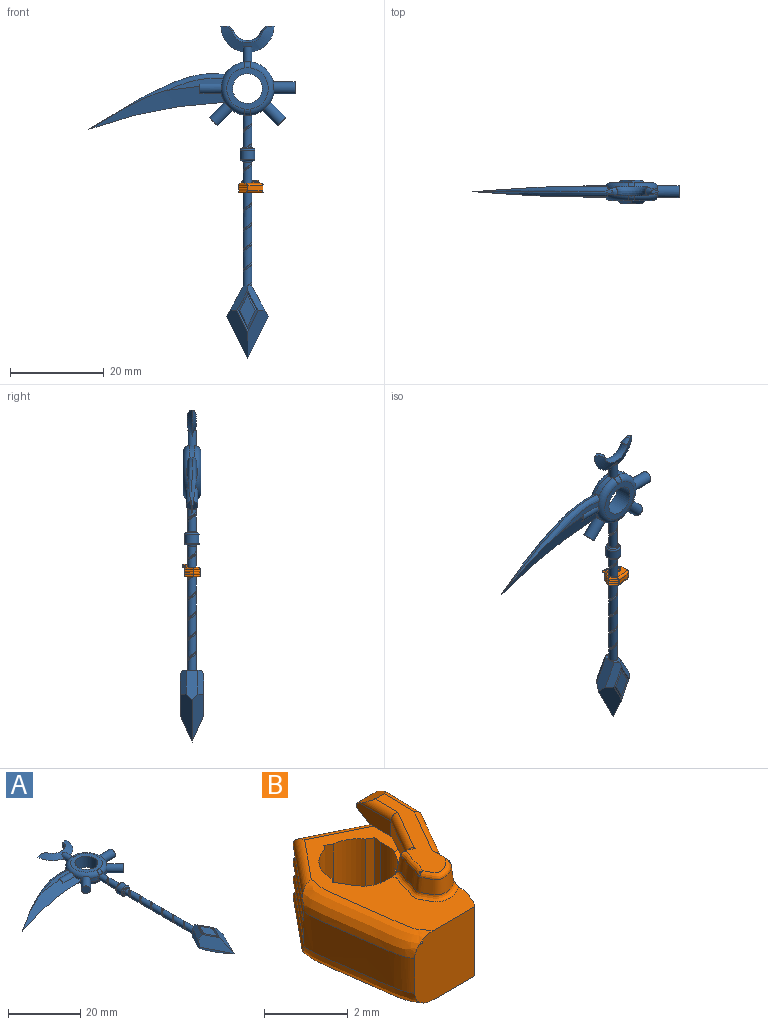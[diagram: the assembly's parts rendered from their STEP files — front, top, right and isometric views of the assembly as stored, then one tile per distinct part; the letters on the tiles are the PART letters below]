
ASSEMBLY  parts=2 mates=1
PART A: 95 faces, bbox 47.1x71.3x5.4 mm
  f0: cylinder r=0.95mm len=6.92mm, axis (0,1,0), area 36.3mm2, adj f1,f2,f3,f6,f20,f23,f67,f69
  f1: bspline ~8.16x2.41mm, area 3.9mm2, adj f0,f2,f3,f37,f38,f67,f68,f69
  f2: bspline ~8.15x2.45mm, area 3.9mm2, adj f0,f1,f20,f37,f38,f67
  f3: cylinder r=5.71mm len=2.59mm, axis (0,0,-1), area 3.2mm2, adj f0,f1,f12,f13,f35,f37
  f4: cylinder r=5.71mm len=2.11mm, axis (0,0,-1), area 0.8mm2, adj f13,f35,f40,f44
  f5: cylinder r=3.17mm len=6.35mm, axis (0,0,-1), area 76mm2, adj f16,f17
  f6: cylinder r=5.71mm len=2.59mm, axis (0,0,-1), area 3.2mm2, adj f0,f8,f9,f33
  f7: cylinder r=5.71mm len=2.11mm, axis (0,0,-1), area 2.6mm2, adj f8,f9,f25,f33
  f8: torus R=4.45mm, axis (0,0,1), area 28.3mm2, adj f6,f7,f15,f17,f20,f21,f25,f33
  f9: torus R=4.45mm, axis (0,0,1), area 28.3mm2, adj f6,f7,f15,f16,f22,f23,f25,f33
  f10: cylinder r=5.71mm len=4.27mm, axis (0,0,-1), area 6.4mm2, adj f12,f13,f19,f41,f42
  f11: cylinder r=5.71mm len=2.11mm, axis (0,0,-1), area 0.8mm2, adj f12,f35,f39,f45
  f12: torus R=4.45mm, axis (0,0,1), area 27.6mm2, adj f3,f10,f11,f17,f20,f21,f32,f35
  f13: torus R=4.45mm, axis (0,0,1), area 27.7mm2, adj f3,f4,f10,f16,f22,f23,f31,f35
  f14: plane 1.74x0.58mm, normal (0,1,0), area 0.4mm2, adj f19,f26
  f15: cylinder r=5.71mm len=4.87mm, axis (0,0,-1), area 8.6mm2, adj f8,f9,f19,f25
  f16: plane 8.97x8.89mm, normal (0,0,1), area 30.4mm2, adj f5,f9,f13,f22,f23
  f17: plane 8.97x8.89mm, normal (0,0,-1), area 30.4mm2, adj f5,f8,f12,f20,f21
  f18: plane 1.66x0.52mm, normal (0,1,0), area 0.4mm2, adj f19,f27
  f19: cylinder r=0.95mm len=3.3mm, axis (0,1,0), area 18.3mm2, adj f10,f14,f15,f18,f21,f22,f26,f27
  f20: bspline ~1.53x1.35mm, area 2.3mm2, adj f0,f2,f8,f12,f17,f37
  f21: bspline ~1.42x1.3mm, area 2.3mm2, adj f8,f12,f17,f19
  f22: bspline ~1.42x1.3mm, area 2.3mm2, adj f9,f13,f16,f19
  f23: bspline ~1.42x1.3mm, area 2.3mm2, adj f0,f9,f13,f16
  f24: plane 2.54x2.54mm, normal (1,0,0), area 5.1mm2, adj f25
  f25: cylinder r=1.27mm len=4.58mm, axis (-1,0,0), area 36.3mm2, adj f7,f8,f9,f15,f24
  f26: bspline ~11.33x5.46mm, area 29.7mm2, adj f14,f19,f27,f28,f29,f30,f93,f94
  f27: bspline ~11.33x5.46mm, area 30.2mm2, adj f18,f19,f26,f28,f29,f30,f93,f94
  f28: plane 1.88x1.27mm, normal (0.01,1,0), area 0.8mm2, adj f26,f27,f94
  f29: plane 1.84x1.25mm, normal (0.01,1,0), area 0.7mm2, adj f26,f27,f93
  f30: bspline ~7.14x7.14mm, area 18.5mm2, adj f26,f27,f93,f94
  f31: plane 12.18x2.8mm, normal (0,0,1), area 11.7mm2, adj f13,f40,f41,f43,f44
  f32: plane 12.19x2.81mm, normal (0,0,-1), area 11.7mm2, adj f12,f39,f42,f45,f46
  f33: cylinder r=1.27mm len=5.04mm, axis (-0.71,0.71,0), area 36.3mm2, adj f6,f7,f8,f9,f34
  f34: plane 2.54x1.8mm, normal (0.71,-0.71,0), area 5.1mm2, adj f33
  f35: cylinder r=1.27mm len=5.06mm, axis (0.71,0.71,0), area 36.2mm2, adj f3,f4,f11,f12,f13,f36
  f36: plane 2.54x1.8mm, normal (-0.71,-0.71,0), area 5.1mm2, adj f35
  f37: bspline ~2.13x1.59mm, area 0.5mm2, adj f1,f2,f3,f12,f20,f38
  f38: plane 0.71x0.37mm, normal (0,0,-1), area 0.1mm2, adj f1,f2,f37
  f39: bspline ~33.29x10.15mm, area 73.1mm2, adj f11,f32,f40,f42,f45,f46
  f40: bspline ~33.29x10.15mm, area 73mm2, adj f4,f31,f39,f41,f43,f44
  f41: bspline ~30.28x13.43mm, area 35.4mm2, adj f10,f13,f31,f40,f42
  f42: bspline ~30.28x13.43mm, area 35.4mm2, adj f10,f12,f32,f39,f41
  f43: plane 1.87x0.64mm, normal (-1,0,0), area 0.5mm2, adj f31,f40,f44
  f44: cylinder r=1.27mm len=4.58mm, axis (1,0,0), area 10.1mm2, adj f4,f13,f31,f40,f43
  f45: cylinder r=1.27mm len=4.58mm, axis (1,0,0), area 10.1mm2, adj f11,f12,f32,f39,f46
  f46: plane 1.87x0.64mm, normal (-1,0,0), area 0.5mm2, adj f32,f39,f45
  f47: plane 2.57x2.57mm, normal (0,1,0), area 0.2mm2, adj f67,f68,f69,f74
  f48: plane 2.57x2.57mm, normal (0,-1,0), area 0.2mm2, adj f70,f71,f72,f73
  f49: cylinder r=1.59mm len=3.18mm, axis (0,-1,0), area 19.3mm2, adj f73,f74
  f50: plane 10.2x4.46mm, normal (-0.63,-0.32,0.71), area 28.3mm2, adj f51,f53,f57,f58,f78
  f51: plane 10.2x4.46mm, normal (-0.63,-0.32,-0.71), area 28.3mm2, adj f50,f52,f55,f58,f84
  f52: plane 5.16x3.72mm, normal (-0.62,0.34,-0.71), area 10.1mm2, adj f51,f54,f58,f59,f85
  f53: plane 10.2x4.46mm, normal (0.63,-0.32,0.71), area 28.3mm2, adj f50,f55,f56,f61,f79
  f54: plane 5.16x3.72mm, normal (0.62,0.34,-0.71), area 10.1mm2, adj f52,f55,f60,f61,f86
  f55: plane 10.2x4.46mm, normal (0.63,-0.32,-0.71), area 28.3mm2, adj f51,f53,f54,f61,f91
  f56: plane 5.16x3.72mm, normal (0.62,0.34,0.71), area 10.1mm2, adj f53,f57,f61,f62,f80
  f57: plane 5.16x3.72mm, normal (-0.62,0.34,0.71), area 10.1mm2, adj f50,f56,f58,f63,f81
  f58: plane 6.48x3.56mm, normal (-0.88,0.48,0), area 16.7mm2, adj f50,f51,f52,f57,f59,f63,f66
  f59: plane 1.93x0.96mm, normal (-0.06,1,0), area 0.9mm2, adj f52,f58,f60,f66
  f60: plane 1.93x0.96mm, normal (0.06,1,0), area 0.9mm2, adj f54,f59,f61,f66
  f61: plane 6.48x3.56mm, normal (0.88,0.48,0), area 16.7mm2, adj f53,f54,f55,f56,f60,f62,f66
  f62: plane 1.94x0.96mm, normal (0.06,1,0), area 0.9mm2, adj f56,f61,f63,f64,f65,f66
  f63: plane 1.93x0.95mm, normal (-0.06,1,0), area 0.9mm2, adj f57,f58,f62,f64,f66
  f64: bspline ~28x2.45mm, area 13.4mm2, adj f62,f63,f65,f66,f70,f71,f72
  f65: bspline ~28.02x2.41mm, area 13.8mm2, adj f62,f64,f66,f71
  f66: cylinder r=0.95mm len=26.59mm, axis (0,1,0), area 134.4mm2, adj f58,f59,f60,f61,f62,f63,f64,f65
  f67: bspline ~0.85x0.81mm, area 0.2mm2, adj f0,f1,f2,f47,f68,f69
  f68: bspline ~0.61x0.46mm, area 0.1mm2, adj f1,f47,f67,f69
  f69: torus R=1.26mm, axis (0,-1,0), area 3mm2, adj f0,f1,f47,f67,f68
  f70: bspline ~0.57x0.49mm, area 0.1mm2, adj f48,f64,f71,f72
  f71: bspline ~0.85x0.75mm, area 0.2mm2, adj f48,f64,f65,f66,f70,f72
  f72: torus R=1.26mm, axis (0,-1,0), area 3mm2, adj f48,f64,f66,f70,f71
  f73: torus R=1.28mm, axis (0,-1,0), area 4.4mm2, adj f48,f49
  f74: torus R=1.28mm, axis (0,-1,0), area 4.4mm2, adj f47,f49
  f75: plane 3.66x2mm, normal (-0.62,0.34,0.71), area 1.4mm2, adj f76,f81,f82,f83
  f76: plane 3.66x2mm, normal (0.62,0.34,0.71), area 1.4mm2, adj f75,f77,f80,f83
  f77: plane 3.96x2mm, normal (0.63,-0.32,0.71), area 1.5mm2, adj f76,f79,f82,f83
  f78: plane 4.53x2.28mm, normal (0.63,0.32,0.71), area 1.7mm2, adj f50,f79,f81,f82
  f79: plane 4.53x2.28mm, normal (-0.63,0.32,0.71), area 1.7mm2, adj f53,f77,f78,f80
  f80: plane 4.18x2.28mm, normal (-0.62,-0.34,0.71), area 1.6mm2, adj f56,f76,f79,f81
  f81: plane 4.18x2.28mm, normal (0.62,-0.34,0.71), area 1.6mm2, adj f57,f75,f78,f80
  f82: plane 3.96x2mm, normal (-0.63,-0.32,0.71), area 1.5mm2, adj f75,f77,f78,f83
  f83: plane 6.52x3.42mm, normal (0,0,1), area 11.1mm2, adj f75,f76,f77,f82
  f84: plane 4.53x2.28mm, normal (0.63,0.32,-0.71), area 1.7mm2, adj f51,f85,f90,f91
  f85: plane 4.18x2.28mm, normal (0.62,-0.34,-0.71), area 1.6mm2, adj f52,f84,f86,f89
  f86: plane 4.18x2.28mm, normal (-0.62,-0.34,-0.71), area 1.6mm2, adj f54,f85,f88,f91
  f87: plane 3.96x2mm, normal (0.63,-0.32,-0.71), area 1.5mm2, adj f88,f90,f91,f92
  f88: plane 3.66x2mm, normal (0.62,0.34,-0.71), area 1.4mm2, adj f86,f87,f89,f92
  f89: plane 3.66x2mm, normal (-0.62,0.34,-0.71), area 1.4mm2, adj f85,f88,f90,f92
  f90: plane 3.96x2mm, normal (-0.63,-0.32,-0.71), area 1.5mm2, adj f84,f87,f89,f92
  f91: plane 4.53x2.28mm, normal (-0.63,0.32,-0.71), area 1.7mm2, adj f55,f84,f86,f87
  f92: plane 6.52x3.42mm, normal (0,0,-1), area 11.1mm2, adj f87,f88,f89,f90
  f93: bspline ~2.68x1.63mm, area 2.6mm2, adj f26,f27,f29,f30
  f94: bspline ~2.79x1.69mm, area 2.8mm2, adj f26,f27,f28,f30
PART B: 79 faces, bbox 4.3x5.7x2.9 mm
  f0: plane 4.84x2.76mm, normal (0,0,-1), area 6.7mm2, adj f5,f6,f7,f8,f9,f10,f12,f16
  f1: plane 0.22x0.13mm, normal (-0.98,0.2,0), area 0mm2, adj f10,f19,f23,f76
  f2: plane 0.22x0.13mm, normal (-0.98,0.2,0), area 0mm2, adj f25,f29,f30,f76
  f3: plane 0.22x0.13mm, normal (-0.98,0.2,0), area 0mm2, adj f32,f36,f37,f76
  f4: plane 0.22x0.13mm, normal (-0.98,0.2,0), area 0mm2, adj f39,f43,f44,f76
  f5: plane 2.03x0.23mm, normal (-0.98,0.2,0), area 0.5mm2, adj f0,f7,f11,f76
  f6: plane 2.03x0.21mm, normal (-0.51,-0.86,0), area 0.5mm2, adj f0,f9,f11,f78
  f7: plane 2.03x0.2mm, normal (-0.51,-0.86,0), area 0.5mm2, adj f0,f5,f11,f78
  f8: plane 2.03x0.12mm, normal (0.8,-0.6,0), area 0.3mm2, adj f0,f11,f12,f77
  f9: plane 2.03x0.14mm, normal (0.8,-0.6,0), area 0.4mm2, adj f0,f6,f11,f77
  f10: plane 0.47x0.41mm, normal (-0.04,-0.5,-0.87), area 0.2mm2, adj f0,f1,f19,f24,f76
  f11: plane 4.94x2.78mm, normal (0,0,1), area 5.2mm2, adj f5,f6,f7,f8,f9,f12,f16,f17
  f12: extruded ~2.03x2.02mm, area 5mm2, adj f0,f8,f11,f17,f48,f69
  f13: extruded ~0.41x0.37mm, area 0.1mm2, adj f18,f35,f42,f46
  f14: extruded ~0.51x0.37mm, area 0.1mm2, adj f18,f28,f35
  f15: extruded ~0.41x0.37mm, area 0.1mm2, adj f18,f22,f28,f47
  f16: plane 2.18x2.18mm, normal (0,-1,0), area 4mm2, adj f0,f11,f17,f18,f46,f47
  f17: extruded ~2.05x2.01mm, area 4.2mm2, adj f0,f11,f12,f16,f48,f70,f72
  f18: extruded ~3.28x1.02mm, area 3.4mm2, adj f13,f14,f15,f16,f46,f47
  f19: plane 0.48x0.07mm, normal (-0.07,-1,0), area 0mm2, adj f1,f10,f23,f24
  f20: cylinder r=0.25mm len=1.12mm, axis (0.14,0.99,0), area 0.9mm2, adj f0,f21,f24,f26
  f21: cylinder r=0.25mm len=1.76mm, axis (-0.9,0.44,0), area 1.5mm2, adj f0,f20,f22,f27
  f22: cylinder r=0.25mm len=2.02mm, axis (-0.64,-0.77,0), area 1.7mm2, adj f0,f15,f21,f28,f47
  f23: plane 0.47x0.41mm, normal (-0.04,-0.5,0.87), area 0.2mm2, adj f1,f19,f24,f29,f76
  f24: bspline ~0.52x0.38mm, area 0.2mm2, adj f10,f19,f20,f23
  f25: plane 0.48x0.07mm, normal (-0.07,-1,0), area 0mm2, adj f2,f29,f30,f31
  f26: cylinder r=0.25mm len=1.12mm, axis (0.14,0.99,0), area 0.9mm2, adj f20,f27,f31,f33
  f27: cylinder r=0.25mm len=1.76mm, axis (-0.9,0.44,0), area 1.5mm2, adj f21,f26,f28,f34
  f28: cylinder r=0.25mm len=1.88mm, axis (-0.64,-0.77,0), area 1.7mm2, adj f14,f15,f22,f27,f35
  f29: plane 0.47x0.41mm, normal (-0.04,-0.5,-0.87), area 0.2mm2, adj f2,f23,f25,f31,f76
  f30: plane 0.47x0.41mm, normal (-0.04,-0.5,0.87), area 0.2mm2, adj f2,f25,f31,f36,f76
  f31: bspline ~0.52x0.38mm, area 0.2mm2, adj f25,f26,f29,f30
  f32: plane 0.48x0.07mm, normal (-0.07,-1,0), area 0mm2, adj f3,f36,f37,f38
  f33: cylinder r=0.25mm len=1.12mm, axis (0.14,0.99,0), area 0.9mm2, adj f26,f34,f38,f40
  f34: cylinder r=0.25mm len=1.76mm, axis (-0.9,0.44,0), area 1.5mm2, adj f27,f33,f35,f41
  f35: cylinder r=0.25mm len=1.88mm, axis (-0.64,-0.77,0), area 1.7mm2, adj f13,f14,f28,f34,f42
  f36: plane 0.47x0.41mm, normal (-0.04,-0.5,-0.87), area 0.2mm2, adj f3,f30,f32,f38,f76
  f37: plane 0.47x0.41mm, normal (-0.04,-0.5,0.87), area 0.2mm2, adj f3,f32,f38,f43,f76
  f38: bspline ~0.52x0.38mm, area 0.2mm2, adj f32,f33,f36,f37
  f39: plane 0.48x0.07mm, normal (-0.07,-1,0), area 0mm2, adj f4,f43,f44,f45
  f40: cylinder r=0.25mm len=1.3mm, axis (-0.14,-0.99,0), area 1mm2, adj f11,f33,f41,f45,f48
  f41: cylinder r=0.25mm len=2.11mm, axis (0.9,-0.44,0), area 1.7mm2, adj f11,f34,f40,f42,f48
  f42: cylinder r=0.25mm len=2.02mm, axis (0.64,0.77,0), area 1.7mm2, adj f11,f13,f35,f41,f46
  f43: plane 0.47x0.41mm, normal (-0.04,-0.5,-0.87), area 0.2mm2, adj f4,f37,f39,f45,f76
  f44: plane 0.48x0.41mm, normal (-0.04,-0.5,0.87), area 0.2mm2, adj f4,f11,f39,f45,f48,f76
  f45: bspline ~0.52x0.38mm, area 0.2mm2, adj f39,f40,f43,f44
  f46: bspline ~4.29x1.18mm, area 2.8mm2, adj f11,f13,f16,f18,f42
  f47: bspline ~4.29x1.18mm, area 2.8mm2, adj f0,f15,f16,f18,f22
  f48: plane 2.43x1.13mm, normal (0,0,-1), area 1mm2, adj f12,f17,f40,f41,f44,f54,f56,f61
  f49: extruded ~0.25x0.05mm, area 0mm2, adj f51,f54,f57,f69
  f50: plane 0.25x0.17mm, normal (0.87,-0.5,0), area 0mm2, adj f52,f55,f58,f70
  f51: bspline ~1.04x0.65mm, area 0mm2, adj f49,f62,f66,f69
  f52: cylinder r=0.19mm len=0.24mm, axis (-0.5,-0.87,0), area 0mm2, adj f50,f53,f70
  f53: cylinder r=0.19mm len=1.64mm, axis (-0.5,-0.87,0), area 0.5mm2, adj f52,f58,f62,f67,f70
  f54: bspline ~3.19x1.76mm, area 0.3mm2, adj f11,f48,f49,f57,f61,f69
  f55: cylinder r=0.19mm len=0.14mm, axis (0.5,0.87,0), area 0mm2, adj f50,f56,f70
  f56: cylinder r=0.19mm len=1.64mm, axis (0.5,0.87,0), area 0.5mm2, adj f48,f55,f58,f68,f70
  f57: plane 1.26x0.73mm, normal (-0.87,0.5,0), area 0.5mm2, adj f49,f54,f61,f66
  f58: plane 1.54x0.89mm, normal (0.87,-0.5,0), area 0.5mm2, adj f50,f53,f56,f59
  f59: plane 1.54x0.25mm, normal (1,-0.03,0), area 0.4mm2, adj f58,f60,f63,f64,f67,f68
  f60: plane 0.7x0.13mm, normal (0,1,0), area 0.1mm2, adj f59,f61,f63,f64
  f61: plane 1.42x0.45mm, normal (-1,0,0), area 0.5mm2, adj f11,f48,f54,f57,f60,f63,f64,f65
  f62: plane 3.34x1.7mm, normal (0,0,1), area 1.5mm2, adj f51,f53,f64,f65,f66,f67,f69,f70
  f63: plane 0.84x0.58mm, normal (0,0.5,-0.87), area 0.3mm2, adj f48,f59,f60,f61,f68
  f64: plane 0.84x0.58mm, normal (0,0.5,0.87), area 0.3mm2, adj f59,f60,f61,f62,f65,f67
  f65: cylinder r=0.19mm len=1.1mm, axis (0,1,0), area 0.3mm2, adj f61,f62,f64,f66
  f66: cylinder r=0.19mm len=1.4mm, axis (0.5,0.87,0), area 0.4mm2, adj f51,f57,f62,f65
  f67: cylinder r=0.19mm len=1.44mm, axis (-0.03,-1,0), area 0.4mm2, adj f53,f59,f62,f64
  f68: cylinder r=0.19mm len=1.44mm, axis (0.03,1,0), area 0.4mm2, adj f48,f56,f59,f63
  f69: bspline ~0.7x0.69mm, area 0.2mm2, adj f12,f49,f51,f54,f62,f71,f72,f75
  f70: bspline ~0.95x0.69mm, area 0.3mm2, adj f17,f50,f52,f53,f55,f56,f62,f71
  f71: bspline ~1.52x1.01mm, area 0.9mm2, adj f69,f70,f72,f73,f74,f75
  f72: bspline ~1.93x1.43mm, area 0.4mm2, adj f11,f17,f69,f70,f71
  f73: bspline ~1.05x0.52mm, area 0.2mm2, adj f62,f70,f71,f74
  f74: bspline ~0.13x0.11mm, area 0mm2, adj f71,f73,f75
  f75: bspline ~1.01x0.41mm, area 0.2mm2, adj f62,f69,f71,f74
  f76: cylinder r=0.95mm len=2.03mm, axis (0,0,-1), area 1.4mm2, adj f0,f1,f2,f3,f4,f5,f10,f11
  f77: cylinder r=0.95mm len=2.03mm, axis (0,0,-1), area 2.7mm2, adj f0,f8,f9,f11
  f78: cylinder r=0.95mm len=2.03mm, axis (0,0,-1), area 1.7mm2, adj f0,f6,f7,f11
PLACE A rot(axis=(1,0,0),90deg) t=(-9.89,-21.28,26.33)mm fixed
PLACE B rot(axis=(0,0,1),90deg) t=(-9.89,-21.28,-4.96)mm
MATE slider A.f0 <-> B.f76  axis (0,0,1) through (-9.89,-21.28,-11.74)mm
